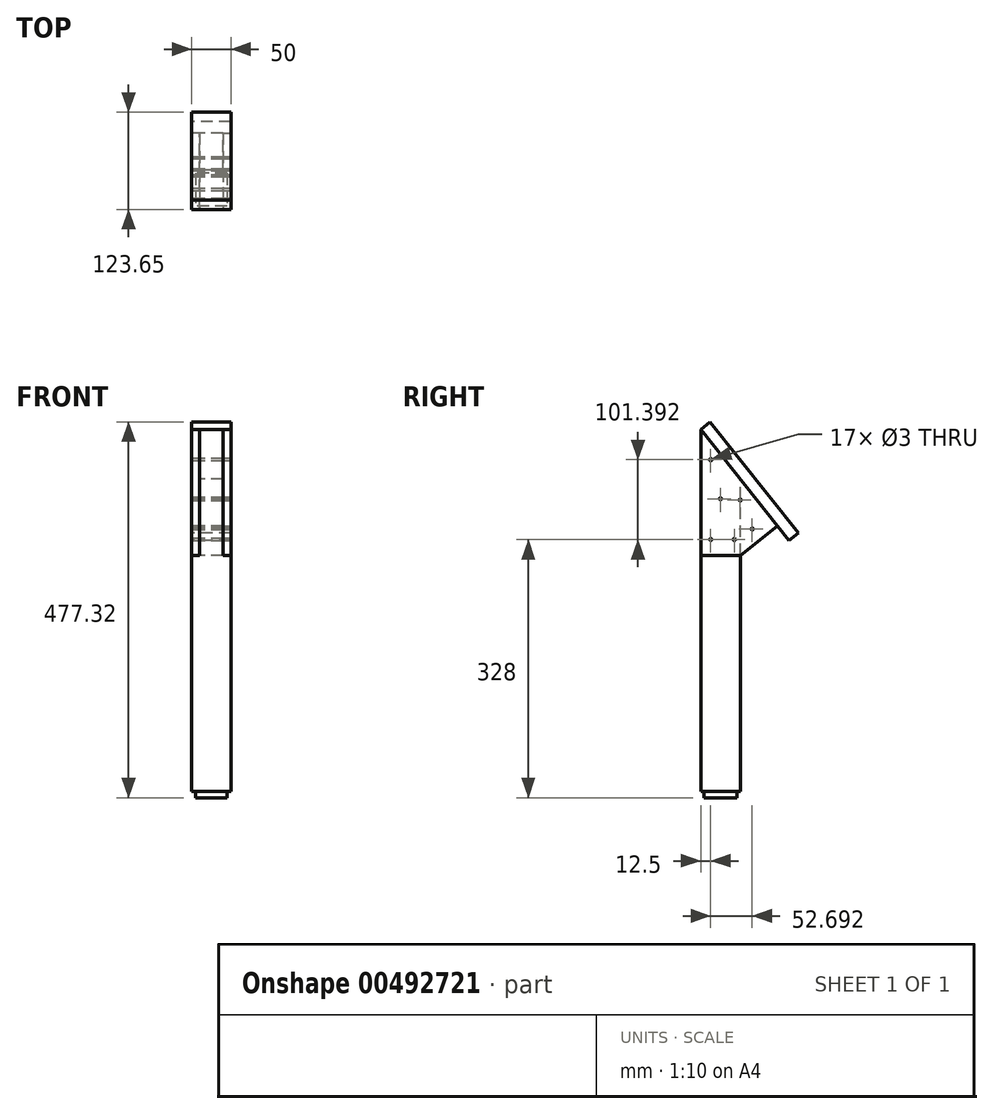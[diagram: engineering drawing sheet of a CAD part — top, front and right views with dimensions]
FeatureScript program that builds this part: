
annotation { "Feature Type Name" : "Feature", "Feature Type Description" : "" }
export const myFeature = defineFeature(function(context is Context, id is Id, definition is map)
    precondition{}
    {
        {
            var Q0;
            Q0=qCreatedBy(makeId("Right.planeOp"),FACE);
            var sketch = newSketch(context, id + "F0", { "sketchPlane" : qUnion([Q0])});
            skLineSegment(sketch, "E0", {"start": v(0, 0) * mm, "end": v(-25, 0) * mm});
            skLineSegment(sketch, "E1", {"start": v(-25, 0) * mm, "end": v(-25, 460) * mm});
            skLineSegment(sketch, "E2", {"start": v(0, 0) * mm, "end": v(25, 0) * mm});
            skLineSegment(sketch, "E3", {"start": v(25, 0) * mm, "end": v(25, 397) * mm});
            skLineSegment(sketch, "E4", {"start": v(-25, 460) * mm, "end": v(25, 397) * mm});
            skLineSegment(sketch, "E5", {"start": v(25, 300) * mm, "end": v(-25, 300) * mm});
            skLineSegment(sketch, "E6.bottom", {"start": v(0, 0) * mm, "end": v(-21, 0) * mm});
            skLineSegment(sketch, "E6.top", {"start": v(0, -8) * mm, "end": v(-21, -8) * mm});
            skLineSegment(sketch, "E6.right", {"start": v(-21, 0) * mm, "end": v(-21, -8) * mm});
            skLineSegment(sketch, "E7.MirrorCS", {"start": v(0, -8) * mm, "end": v(21, -8) * mm});
            skLineSegment(sketch, "E8.MirrorCS", {"start": v(21, 0) * mm, "end": v(21, -8) * mm});
            skSolve(sketch);
        }
        {
            var Q0;
            Q0=makeQuery(id+"F0.imprint","IMPRINT",FACE,{"disambiguationData":[TD([[makeQuery(id+"F0.imprint","IMPRINT",EDGE,{"derivedFrom":sQuery(id+"F0.wireOp",EDGE,"E6.top")}),-1.0]])]});
            extrude(context, id + "F1", {"entities" : qUnion([Q0]), "depth" : 40 * mm, "offsetDistance" : 25 * mm, "symmetric" : true});
        }
        {
            var Q0;
            {var subQ6=sQuery(id+"F0.wireOp",EDGE,"E5");Q0=makeQuery(id+"F0.imprint","IMPRINT",FACE,{"disambiguationData":[TD([[makeQuery(id+"F0.imprint","IMPRINT",EDGE,{"derivedFrom":subQ6}),1.0]])]});}
            extrude(context, id + "F2", {"entities" : qUnion([Q0]), "operationType" : NewBodyOperationType.ADD, "depth" : 50 * mm, "symmetric" : true});
        }
        {
            var Q0;
            {var subQ0=sQuery(id+"F0.wireOp",EDGE,"E4");Q0=makeQuery(id+"F0.imprint","IMPRINT",FACE,{"disambiguationData":[TD([[makeQuery(id+"F0.imprint","IMPRINT",EDGE,{"derivedFrom":subQ0}),-1.0]])]});}
            extrude(context, id + "F3", {"entities" : qUnion([Q0]), "operationType" : NewBodyOperationType.ADD, "depth" : 30 * mm, "symmetric" : true});
        }
        {
            var Q0;
            Q0=makeQuery(id+"F3.opExtrude","CAP_FACE",FACE,{"disambiguationData":[OSD([sQuery(id+"F0.wireOp",EDGE,"E1"),sQuery(id+"F0.wireOp",EDGE,"E3"),sQuery(id+"F0.wireOp",EDGE,"E4"),sQuery(id+"F0.wireOp",EDGE,"E5")])],"isStart":true});
            var sketch = newSketch(context, id + "F4", { "sketchPlane" : qUnion([Q0])});
            skLineSegment(sketch, "E9", {"start": v(-25, 397) * mm, "end": v(-72.23, 337.49) * mm});
            skLineSegment(sketch, "E10", {"start": v(-25, 300) * mm, "end": v(-72.23, 337.49) * mm});
            skLineSegment(sketch, "E11", {"start": v(-25, 397) * mm, "end": v(-25, 300) * mm});
            skSolve(sketch);
        }
        {
            var Q0;
            Q0 = qSketchRegion(id + "F4", true);
            extrude(context, id + "F5", {"entities" : qUnion([Q0]), "oppositeDirection" : true, "depth" : 30 * mm});
        }
        {
            var Q0;
            Q0=makeQuery(id+"F2.opExtrude","CAP_FACE",FACE,{"disambiguationData":[OSD([sQuery(id+"F0.wireOp",EDGE,"E0"),sQuery(id+"F0.wireOp",EDGE,"E1"),sQuery(id+"F0.wireOp",EDGE,"E2"),sQuery(id+"F0.wireOp",EDGE,"E3"),sQuery(id+"F0.wireOp",EDGE,"E5")])],"isStart":true});
            var sketch = newSketch(context, id + "F6", { "sketchPlane" : qUnion([Q0])});
            skLineSegment(sketch, "E12.0.0", {"start": v(25, 300) * mm, "end": v(25, 460) * mm});
            skLineSegment(sketch, "E12.0.1", {"start": v(25, 460) * mm, "end": v(-25, 397) * mm});
            skLineSegment(sketch, "E12.0.3", {"start": v(-25, 300) * mm, "end": v(25, 300) * mm});
            skLineSegment(sketch, "E13.0.0", {"start": v(-72.23, 337.49) * mm, "end": v(-25, 300) * mm});
            skLineSegment(sketch, "E13.0.2", {"start": v(-25, 397) * mm, "end": v(-72.23, 337.49) * mm});
            skSolve(sketch);
        }
        {
            var Q0;
            Q0=makeQuery(id+"F6.imprint","IMPRINT",FACE,{"disambiguationData":[TD([[makeQuery(id+"F6.imprint","IMPRINT",EDGE,{"derivedFrom":sQuery(id+"F6.wireOp",EDGE,"E12.0.0")}),1.0]])]});
            extrude(context, id + "F7", {"entities" : qUnion([Q0]), "oppositeDirection" : true, "depth" : 10 * mm});
        }
        {
            var Q0;
            Q0=makeQuery(id+"F2.opExtrude","CAP_FACE",FACE,{"disambiguationData":[OSD([sQuery(id+"F0.wireOp",EDGE,"E0"),sQuery(id+"F0.wireOp",EDGE,"E1"),sQuery(id+"F0.wireOp",EDGE,"E2"),sQuery(id+"F0.wireOp",EDGE,"E3"),sQuery(id+"F0.wireOp",EDGE,"E5")])],"isStart":false});
            var sketch = newSketch(context, id + "F8", { "sketchPlane" : qUnion([Q0])});
            skLineSegment(sketch, "E14.0.0", {"start": v(-25, 460) * mm, "end": v(-25, 300) * mm});
            skLineSegment(sketch, "E14.0.1", {"start": v(-25, 300) * mm, "end": v(25, 300) * mm});
            skLineSegment(sketch, "E14.0.3", {"start": v(25, 397) * mm, "end": v(-25, 460) * mm});
            skLineSegment(sketch, "E15.0.0", {"start": v(25, 300) * mm, "end": v(72.23, 337.49) * mm});
            skLineSegment(sketch, "E15.0.1", {"start": v(72.23, 337.49) * mm, "end": v(25, 397) * mm});
            skSolve(sketch);
        }
        {
            var Q0;
            Q0 = qSketchRegion(id + "F8", true);
            extrude(context, id + "F9", {"entities" : qUnion([Q0]), "oppositeDirection" : true, "depth" : 10 * mm});
        }
        {
            var Q0;
            Q0=makeQuery(id+"F7.opExtrude","CAP_FACE",FACE,{"disambiguationData":[OSD([sQuery(id+"F6.wireOp",EDGE,"E12.0.0"),sQuery(id+"F6.wireOp",EDGE,"E12.0.1"),sQuery(id+"F6.wireOp",EDGE,"E12.0.3"),sQuery(id+"F6.wireOp",EDGE,"E13.0.0"),sQuery(id+"F6.wireOp",EDGE,"E13.0.2")])],"isStart":true});
            var sketch = newSketch(context, id + "F10", { "sketchPlane" : qUnion([Q0])});
            skCircle(sketch, "E16", {"center": v(12.5, 320) * mm, "radius": 1.5 * mm});
            skCircle(sketch, "E17", {"center": v(12.5, 421.4) * mm, "radius": 1.5 * mm});
            skCircle(sketch, "E18", {"center": v(-17.5, 320) * mm, "radius": 1.5 * mm});
            skCircle(sketch, "E19", {"center": v(0, 371.83) * mm, "radius": 1.5 * mm});
            skCircle(sketch, "E20", {"center": v(-40.2, 333.48) * mm, "radius": 1.5 * mm});
            skCircle(sketch, "E21", {"center": v(-24.96, 370.18) * mm, "radius": 1.5 * mm});
            skSolve(sketch);
        }
        {
            var Q0;
            Q0=makeQuery(id+"F10.imprint","IMPRINT",FACE,{"disambiguationData":[TD([[makeQuery(id+"F10.imprint","IMPRINT",EDGE,{"derivedFrom":sQuery(id+"F10.wireOp",EDGE,"E20")}),1.0]])]});
            var Q1;
            Q1=makeQuery(id+"F10.imprint","IMPRINT",FACE,{"disambiguationData":[TD([[makeQuery(id+"F10.imprint","IMPRINT",EDGE,{"derivedFrom":sQuery(id+"F10.wireOp",EDGE,"E18")}),1.0]])]});
            var Q2;
            Q2=makeQuery(id+"F10.imprint","IMPRINT",FACE,{"disambiguationData":[TD([[makeQuery(id+"F10.imprint","IMPRINT",EDGE,{"derivedFrom":sQuery(id+"F10.wireOp",EDGE,"E16")}),1.0]])]});
            var Q3;
            Q3=makeQuery(id+"F10.imprint","IMPRINT",FACE,{"disambiguationData":[TD([[makeQuery(id+"F10.imprint","IMPRINT",EDGE,{"derivedFrom":sQuery(id+"F10.wireOp",EDGE,"E19")}),1.0]])]});
            var Q4;
            Q4=makeQuery(id+"F10.imprint","IMPRINT",FACE,{"disambiguationData":[TD([[makeQuery(id+"F10.imprint","IMPRINT",EDGE,{"derivedFrom":sQuery(id+"F10.wireOp",EDGE,"E21")}),1.0]])]});
            var Q5;
            Q5=makeQuery(id+"F10.imprint","IMPRINT",FACE,{"disambiguationData":[TD([[makeQuery(id+"F10.imprint","IMPRINT",EDGE,{"derivedFrom":sQuery(id+"F10.wireOp",EDGE,"E17")}),1.0]])]});
            extrude(context, id + "F11", {"entities" : qUnion([Q0, Q1, Q2, Q3, Q4, Q5]), "operationType" : NewBodyOperationType.REMOVE, "endBound" : BoundingType.THROUGH_ALL, "oppositeDirection" : true, "depth" : 25 * mm});
        }
        {
            var Q0;
            Q0=makeQuery(id+"F5.opExtrude","SWEPT_FACE",FACE,{"disambiguationData":[OSD([sQuery(id+"F4.wireOp",EDGE,"E9")])]});
            var sketch = newSketch(context, id + "F12", { "sketchPlane" : qUnion([Q0])});
            skLineSegment(sketch, "E22.0.0", {"start": v(-25, 375.85) * mm, "end": v(-25, 219.45) * mm});
            skLineSegment(sketch, "E22.0.1", {"start": v(-25, 219.45) * mm, "end": v(-15, 219.45) * mm});
            skLineSegment(sketch, "E22.0.2", {"start": v(-15, 219.45) * mm, "end": v(-15, 375.85) * mm});
            skLineSegment(sketch, "E22.0.3", {"start": v(-15, 375.85) * mm, "end": v(-25, 375.85) * mm});
            skLineSegment(sketch, "E23.0.0", {"start": v(25, 219.45) * mm, "end": v(25, 375.85) * mm});
            skLineSegment(sketch, "E23.0.1", {"start": v(25, 375.85) * mm, "end": v(15, 375.85) * mm});
            skLineSegment(sketch, "E23.0.2", {"start": v(15, 375.85) * mm, "end": v(15, 219.45) * mm});
            skLineSegment(sketch, "E23.0.3", {"start": v(15, 219.45) * mm, "end": v(25, 219.45) * mm});
            skPoint(sketch, "E24.oppositeSnap0", {"position": v(25, 297.65) * mm});
            skLineSegment(sketch, "E24.bottom", {"start": v(-25, 375.85) * mm, "end": v(25, 375.85) * mm});
            skLineSegment(sketch, "E24.top", {"start": v(-25, 195.85) * mm, "end": v(25, 195.85) * mm});
            skLineSegment(sketch, "E24.left", {"start": v(-25, 375.85) * mm, "end": v(-25, 195.85) * mm});
            skLineSegment(sketch, "E24.right", {"start": v(25, 375.85) * mm, "end": v(25, 195.85) * mm});
            skSolve(sketch);
        }
        {
            var Q0;
            {var subQ1=sQuery(id+"F4.wireOp",EDGE,"E9");var subQ4=sQuery(id+"F12.wireOp",EDGE,"E22.0.1");var subQ5=makeQuery(id+"F5.opExtrude","SWEPT_EDGE",EDGE,{"disambiguationData":[OSD([subQ1,sQuery(id+"F4.wireOp",EDGE,"E10")])]});var subQ12=makeQuery(id+"F12.imprint","IMPRINT",EDGE,{"derivedFrom":subQ5});var subQ13=sQuery(id+"F12.wireOp",EDGE,"E24.bottom");var subQ19=makeQuery(id+"F12.imprint","IMPRINT",EDGE,{"derivedFrom":subQ4});Q0=qUnion([makeQuery(id+"F12.imprint","IMPRINT",FACE,{"disambiguationData":[TD([[makeQuery(id+"F12.imprint","IMPRINT",EDGE,{"derivedFrom":sQuery(id+"F12.wireOp",EDGE,"E22.0.0")}),1.0]])]}),makeQuery(id+"F12.imprint","IMPRINT",FACE,{"disambiguationData":[TD([[subQ19,-1.0]])]}),makeQuery(id+"F12.imprint","IMPRINT",FACE,{"disambiguationData":[TD([[makeQuery(id+"F12.imprint","IMPRINT",EDGE,{"derivedFrom":subQ13}),-1.0]])]}),makeQuery(id+"F12.imprint","IMPRINT",FACE,{"disambiguationData":[TD([[makeQuery(id+"F12.imprint","IMPRINT",EDGE,{"derivedFrom":sQuery(id+"F12.wireOp",EDGE,"E23.0.0")}),1.0]])]}),makeQuery(id+"F12.imprint","IMPRINT",FACE,{"disambiguationData":[TD([[subQ12,1.0]])]})]);}
            extrude(context, id + "F13", {"entities" : qUnion([Q0]), "depth" : 15 * mm});
        }
    });
